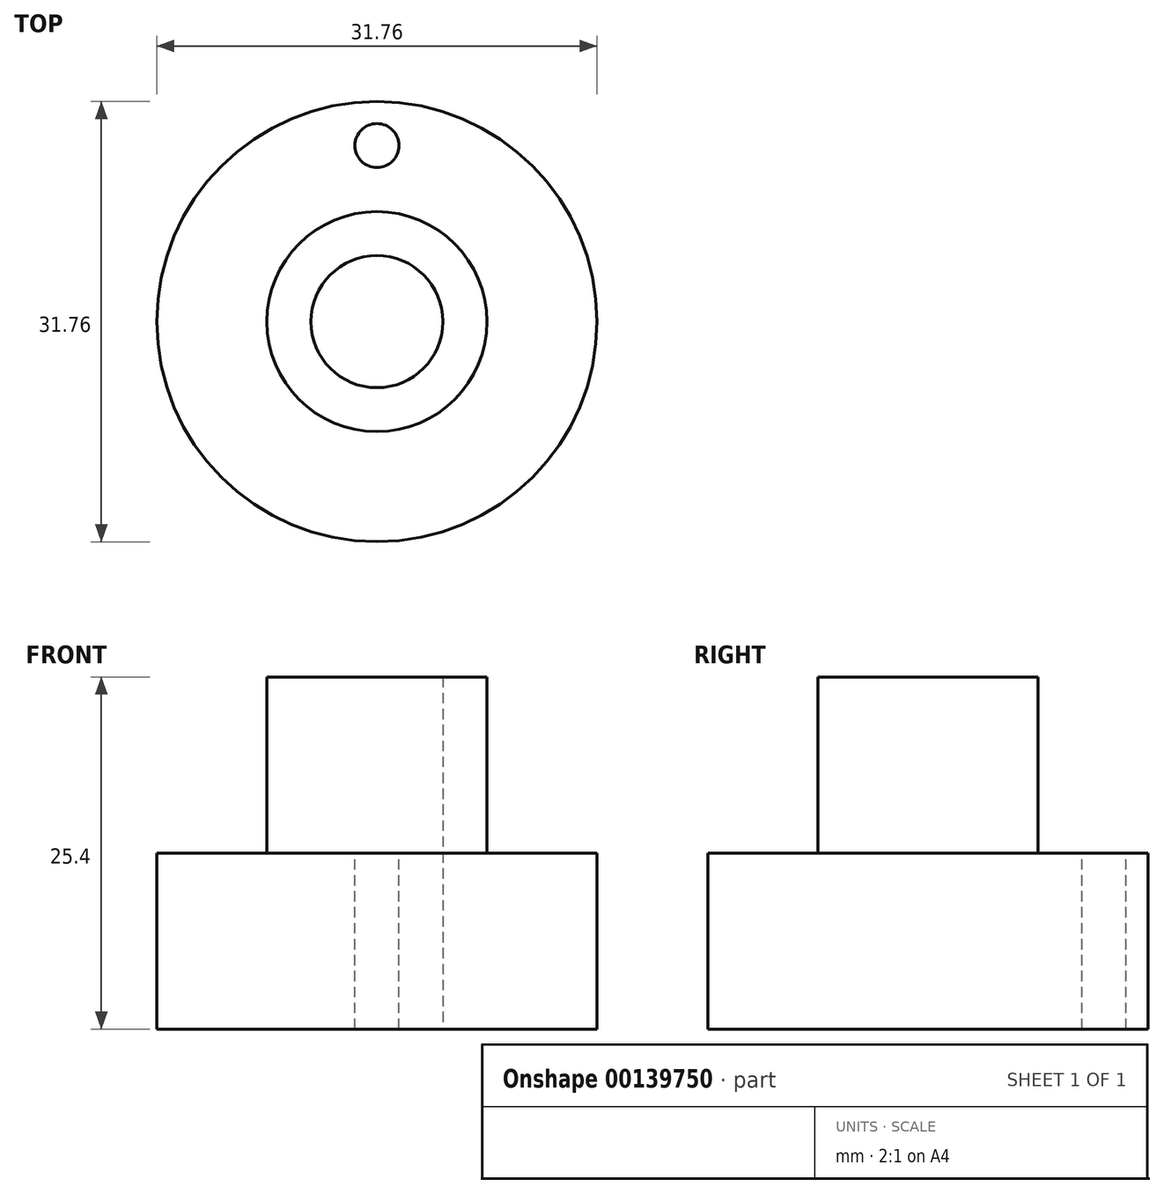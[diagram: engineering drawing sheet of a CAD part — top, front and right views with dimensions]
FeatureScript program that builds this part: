
annotation { "Feature Type Name" : "Feature", "Feature Type Description" : "" }
export const myFeature = defineFeature(function(context is Context, id is Id, definition is map)
    precondition{}
    {
        {
            var Q0;
            Q0=qCreatedBy(makeId("Top.planeOp"),FACE);
            var sketch = newSketch(context, id + "F0", { "sketchPlane" : qUnion([Q0])});
            skCircle(sketch, "E0", {"center": v(0, 0) * mm, "radius": 15.88 * mm});
            skCircle(sketch, "E1", {"center": v(0, 0) * mm, "radius": 12.7 * mm, "construction": true});
            skCircle(sketch, "E2", {"center": v(0, 0) * mm, "radius": 7.94 * mm});
            skCircle(sketch, "E3", {"center": v(0, 0) * mm, "radius": 4.76 * mm});
            skSolve(sketch);
        }
        {
            var Q0;
            Q0 = qSketchRegion(id + "F0", true);
            var Q1;
            Q1=makeQuery(id+"F0.imprint","IMPRINT",FACE,{"disambiguationData":[TD([[makeQuery(id+"F0.imprint","IMPRINT",EDGE,{"derivedFrom":sQuery(id+"F0.wireOp",EDGE,"E2")}),1.0]])]});
            extrude(context, id + "F1", {"entities" : qUnion([Q0, Q1]), "depth" : 12.7 * mm});
        }
        {
            var Q0;
            Q0=makeQuery(id+"F0.imprint","IMPRINT",FACE,{"disambiguationData":[TD([[makeQuery(id+"F0.imprint","IMPRINT",EDGE,{"derivedFrom":sQuery(id+"F0.wireOp",EDGE,"E2")}),1.0]])]});
            extrude(context, id + "F2", {"entities" : qUnion([Q0]), "operationType" : NewBodyOperationType.ADD, "depth" : 25.4 * mm});
        }
        {
            var Q0;
            Q0=makeQuery(id+"F1.opExtrude","CAP_FACE",FACE,{"disambiguationData":[OSD([sQuery(id+"F0.wireOp",EDGE,"E0"),sQuery(id+"F0.wireOp",EDGE,"E3")])],"isStart":false});
            var sketch = newSketch(context, id + "F3", { "sketchPlane" : qUnion([Q0])});
            skCircle(sketch, "E4", {"center": v(0, 0) * mm, "radius": 12.7 * mm, "construction": true});
            skCircle(sketch, "E5", {"center": v(0, 12.7) * mm, "radius": 1.59 * mm});
            skSolve(sketch);
        }
        {
            var Q0;
            Q0=makeQuery(id+"F3.imprint","IMPRINT",FACE,{"disambiguationData":[TD([[makeQuery(id+"F3.imprint","IMPRINT",EDGE,{"derivedFrom":sQuery(id+"F3.wireOp",EDGE,"E5")}),1.0]])]});
            var Q1;
            Q1=sQuery(id+"F3.wireOp",EDGE,"E5");
            extrude(context, id + "F4", {"entities" : qUnion([Q0]), "operationType" : NewBodyOperationType.REMOVE, "surfaceEntities" : qUnion([Q1]), "oppositeDirection" : true, "depth" : 12.7 * mm});
        }
    });
